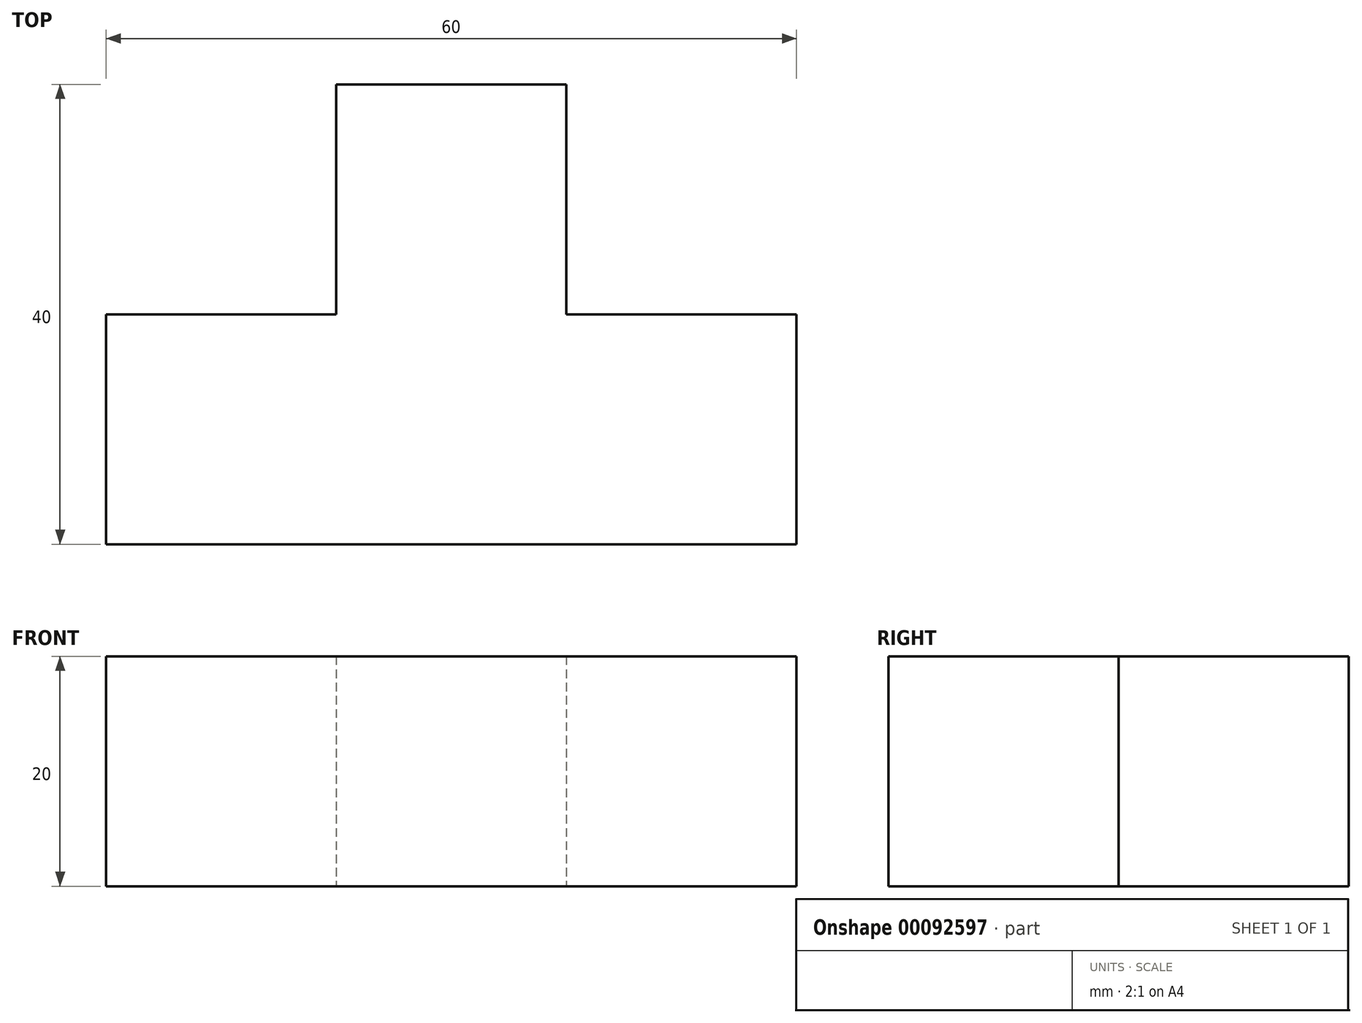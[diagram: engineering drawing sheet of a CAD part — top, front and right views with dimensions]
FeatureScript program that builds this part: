
annotation { "Feature Type Name" : "Feature", "Feature Type Description" : "" }
export const myFeature = defineFeature(function(context is Context, id is Id, definition is map)
    precondition{}
    {
        {
            var Q0;
            Q0=qCreatedBy(makeId("Top.planeOp"),FACE);
            var sketch = newSketch(context, id + "F0", { "sketchPlane" : qUnion([Q0])});
            skLineSegment(sketch, "E0.bottom", {"start": v(-30.33, 5.6) * mm, "end": v(-10.33, 5.6) * mm});
            skLineSegment(sketch, "E0.top", {"start": v(-30.33, -14.4) * mm, "end": v(29.67, -14.4) * mm});
            skLineSegment(sketch, "E0.left", {"start": v(-30.33, 5.6) * mm, "end": v(-30.33, -14.4) * mm});
            skLineSegment(sketch, "E0.right", {"start": v(29.67, 5.6) * mm, "end": v(29.67, -14.4) * mm});
            skLineSegment(sketch, "E1.bottom", {"start": v(-10.33, 25.6) * mm, "end": v(9.67, 25.6) * mm});
            skLineSegment(sketch, "E1.left", {"start": v(-10.33, 25.6) * mm, "end": v(-10.33, 5.6) * mm});
            skLineSegment(sketch, "E1.right", {"start": v(9.67, 25.6) * mm, "end": v(9.67, 5.6) * mm});
            skLineSegment(sketch, "E2.trimOffspring", {"start": v(9.67, 5.6) * mm, "end": v(29.67, 5.6) * mm});
            skSolve(sketch);
        }
        {
            var Q0;
            Q0=makeQuery(id+"F0.imprint","IMPRINT",FACE,{"disambiguationData":[TD([[makeQuery(id+"F0.imprint","IMPRINT",EDGE,{"derivedFrom":sQuery(id+"F0.wireOp",EDGE,"E0.bottom")}),-1.0]])]});
            extrude(context, id + "F1", {"entities" : qUnion([Q0]), "depth" : 20 * mm});
        }
    });
